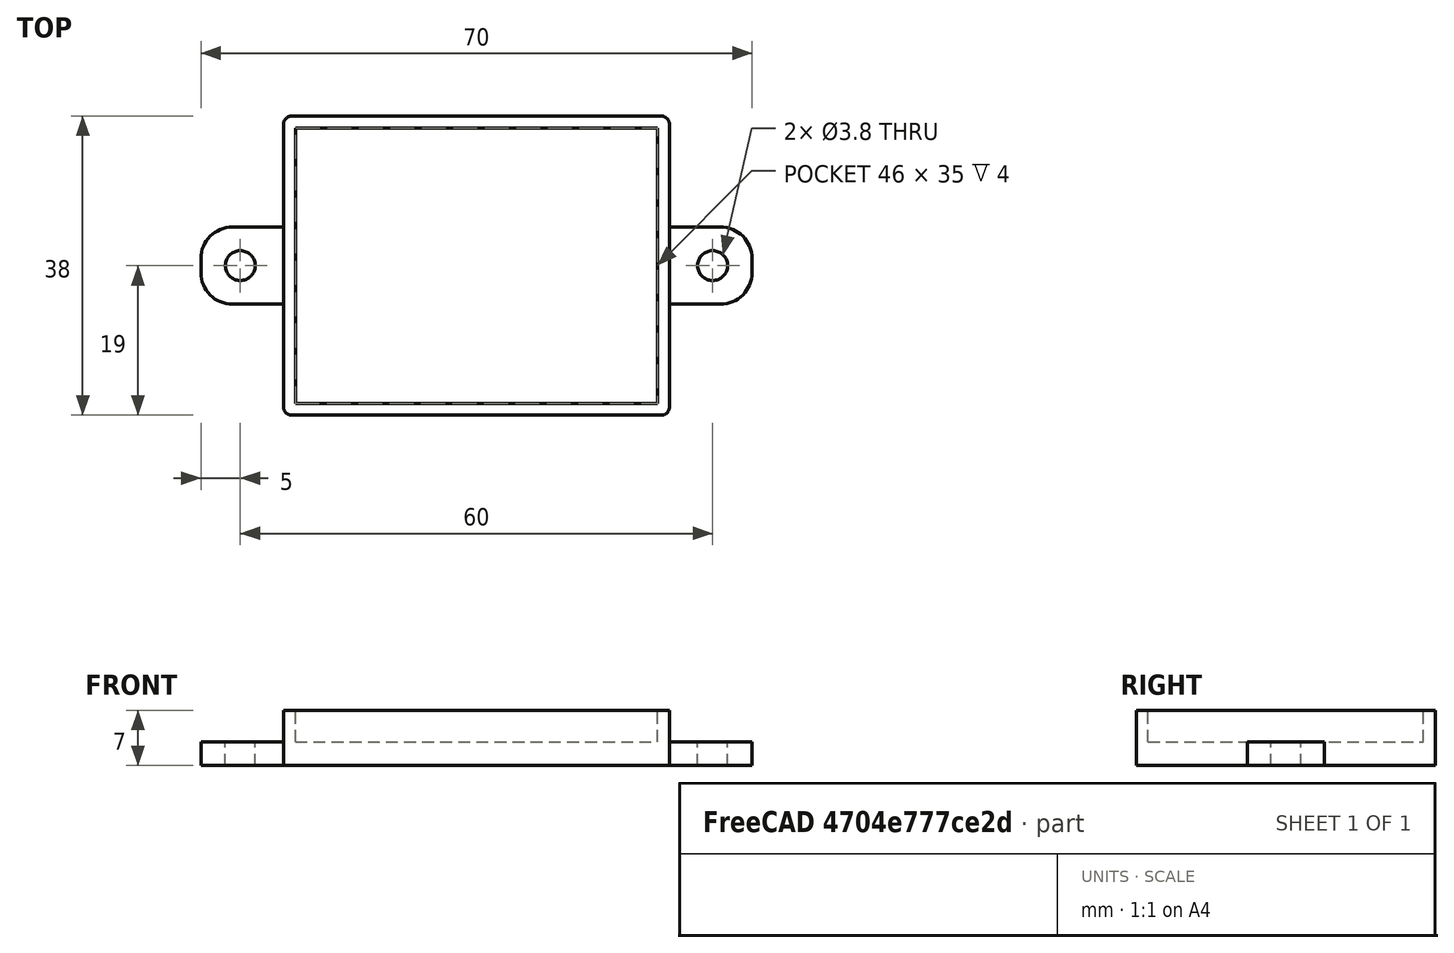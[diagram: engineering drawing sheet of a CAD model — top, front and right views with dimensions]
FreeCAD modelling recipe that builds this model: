
FCSTD DOCUMENT  (FreeCAD 0.18.4R)
Label: bread_board_holder
License: FreeArt
LicenseURL: http://artlibre.org/licence/lal
objects: Part::Box×3, Part::Fillet×2, Part::Cut×2, Spreadsheet::Sheet×1, Part::Cylinder×1, Part::FeaturePython×1, Part::MultiFuse×1
note: 10 computed .brp shape members not serialized (recipe doc carries the construction recipe); baked Part::Feature solids carry a one-line shape summary decoded from their .brp

FEATURE [Spreadsheet::Sheet] Spreadsheet  label="p"
  cells = A1=attach_hole_dist; B1(attach_hole_dist)=10; A2=attach_hole_r; B2(attach_hole_r)=1.9; A3=attach_hole_wall; B3(attach_hole_wall)=3; A4=attach_z; B4(attach_z)=3; A5=side_wall; B5(side_wall)=1.5; A6=bb_x; B6(bb_x)=46; A7=bb_y; B7(bb_y)=35; A8=box_z; B8(box_z)=4; A9=bottom_wall; B9(bottom_wall)==attach_z
FEATURE [Part::Box] Box  label="external cube"
  AttacherType = Attacher::AttachEngine3D
  Height = 7
  Length = 49
  Width = 38
  expr: Length = 2 * p.side_wall + p.bb_x
  expr: Width = 2 * p.side_wall + p.bb_y
  expr: Height = p.bottom_wall + p.box_z
FEATURE [Part::Box] Box001  label="internal cube"
  AttacherType = Attacher::AttachEngine3D
  Height = 4
  Length = 46
  Placement = pos=(1.5,1.5,3) rot=(0,0,1;0rad)
  Width = 35
  expr: Placement.Base.y = p.side_wall
  expr: Placement.Base.x = p.side_wall
  expr: Length = p.bb_x
  expr: Width = p.bb_y
  expr: Placement.Base.z = p.bottom_wall
  expr: Height = p.box_z
FEATURE [Part::Box] Box005  label="ears cube"
  AttacherType = Attacher::AttachEngine3D
  Height = 3
  Length = 70
  Width = 9.8
  expr: Height = p.attach_z
  expr: Length = floor((p.bb_x + 2 * p.side_wall) / p.attach_hole_dist + 3) * p.attach_hole_dist
  expr: Width = (p.attach_hole_r + p.attach_hole_wall) * 2
FEATURE [Part::Fillet] Fillet002  label="ears cube fillet"
  Base = -> Box005
  Edges = 4 edges r=4: [Edge1,Edge3,Edge5,Edge7]
FEATURE [Part::Cylinder] Cylinder001  label="attach hole"
  Angle = 360
  AttacherType = Attacher::AttachEngine3D
  Height = 10
  Placement = pos=(5,4.9,0) rot=(0,0,1;0rad)
  Radius = 1.9
  expr: Placement.Base.x = p.attach_hole_dist / 2
  expr: Placement.Base.y = p.attach_hole_r + p.attach_hole_wall
  expr: Radius = p.attach_hole_r
FEATURE [Part::FeaturePython] Array002  label="attach hole array"  # Draft array (typed FeaturePython)
  Angle = 360
  ArrayType = 0
  Axis = (0,0,1)
  Base = -> Cylinder001
  Center = (0,0,0)
  Fuse = false
  IntervalAxis = (0,0,0)
  IntervalX = (60,0,0)
  IntervalY = (0,1,0)
  IntervalZ = (0,0,1)
  NumberPolar = 1
  NumberX = 2
  NumberY = 1
  NumberZ = 1
  expr: IntervalX.x = floor((p.bb_x + 2 * p.side_wall) / p.attach_hole_dist + 2) * p.attach_hole_dist
FEATURE [Part::Cut] Cut002  label="attach plane"
  Base = -> Fillet002
  Placement = pos=(-10.5,14.1,0) rot=(0,0,1;0rad)
  Tool = -> Array002
  expr: Placement.Base.y = p.side_wall + p.bb_y / 2 - (p.attach_hole_r + p.attach_hole_wall)
  expr: Placement.Base.x = -(floor(p.bb_x / p.attach_hole_dist + 3) * p.attach_hole_dist - p.side_wall * 2 - p.bb_x) / 2
FEATURE [Part::Fillet] Fillet  label="external fillet"
  Base = -> Box
  Edges = 4 edges r=1: [Edge1,Edge3,Edge5,Edge7]
FEATURE [Part::MultiFuse] Fusion  label="external fusion"
  Shapes = -> [Cut002,Fillet]
FEATURE [Part::Cut] Cut  label="bread board cut"
  Base = -> Fusion
  Tool = -> Box001
